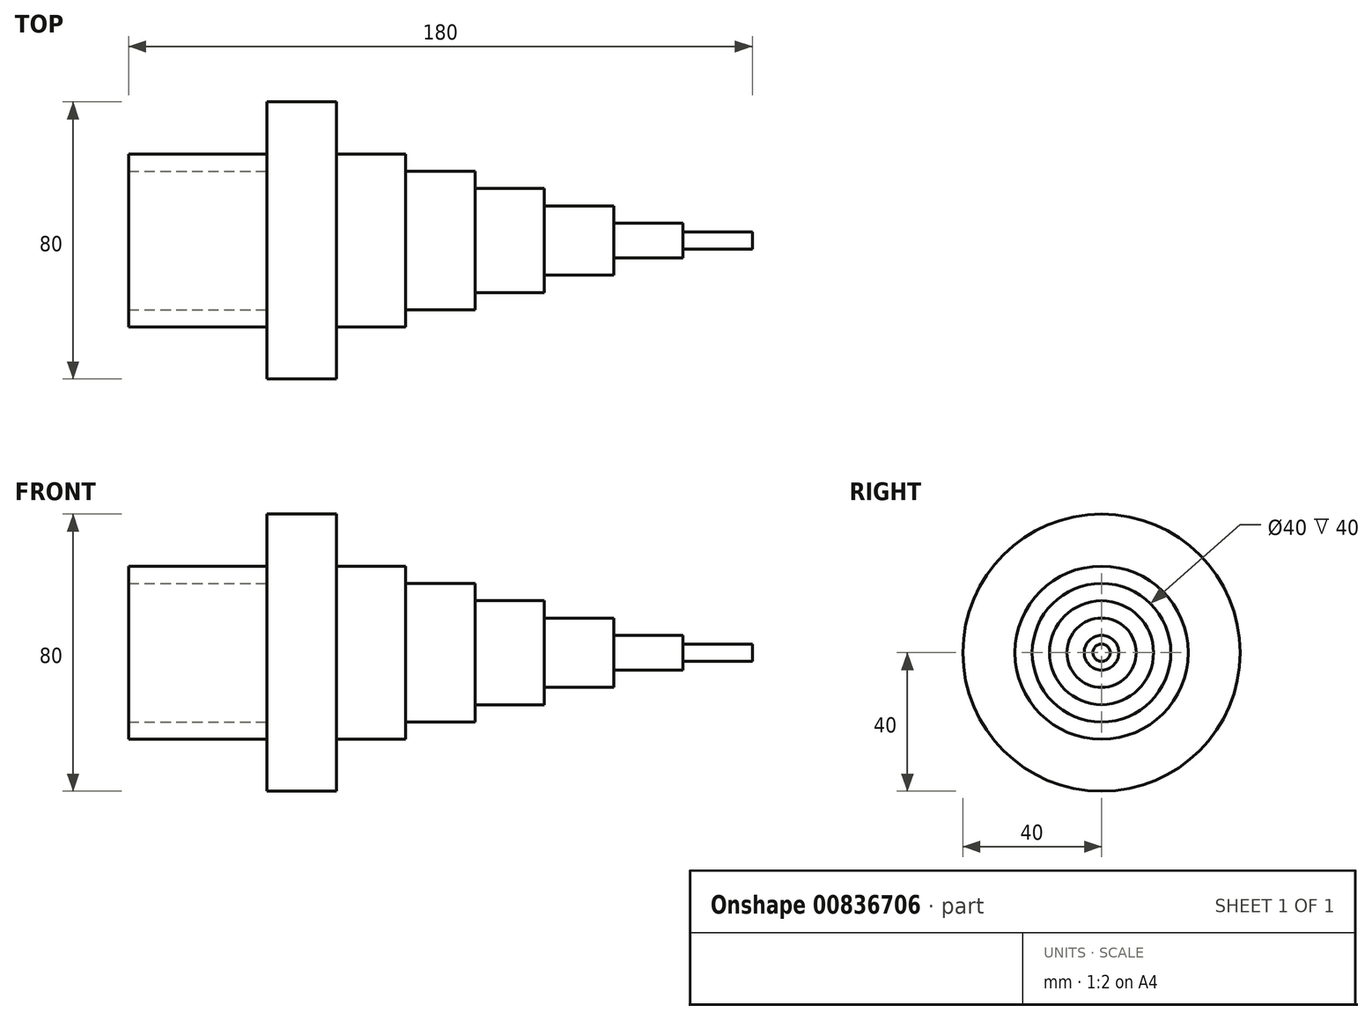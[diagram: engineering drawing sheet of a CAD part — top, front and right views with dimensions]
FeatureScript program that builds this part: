
annotation { "Feature Type Name" : "Feature", "Feature Type Description" : "" }
export const myFeature = defineFeature(function(context is Context, id is Id, definition is map)
    precondition{}
    {
        {
            var Q0;
            Q0=qCreatedBy(makeId("Front.planeOp"),FACE);
            var sketch = newSketch(context, id + "F0", { "sketchPlane" : qUnion([Q0])});
            skLineSegment(sketch, "E0", {"start": v(-45.8, 0) * mm, "end": v(-45.8, 25) * mm});
            skLineSegment(sketch, "E1", {"start": v(-45.8, 25) * mm, "end": v(-5.8, 25) * mm});
            skLineSegment(sketch, "E2", {"start": v(-5.8, 40) * mm, "end": v(-5.8, 25) * mm});
            skLineSegment(sketch, "E3", {"start": v(-5.8, 40) * mm, "end": v(14.2, 40) * mm});
            skLineSegment(sketch, "E4", {"start": v(14.2, 40) * mm, "end": v(14.2, 25) * mm});
            skLineSegment(sketch, "E5", {"start": v(14.2, 25) * mm, "end": v(34.2, 25) * mm});
            skLineSegment(sketch, "E6", {"start": v(34.2, 25) * mm, "end": v(34.2, 20) * mm});
            skLineSegment(sketch, "E7", {"start": v(34.2, 20) * mm, "end": v(54.2, 20) * mm});
            skLineSegment(sketch, "E8", {"start": v(54.2, 20) * mm, "end": v(54.2, 15) * mm});
            skLineSegment(sketch, "E9", {"start": v(54.2, 15) * mm, "end": v(74.2, 15) * mm});
            skLineSegment(sketch, "E10", {"start": v(74.2, 15) * mm, "end": v(74.2, 10) * mm});
            skLineSegment(sketch, "E11", {"start": v(74.2, 10) * mm, "end": v(94.2, 10) * mm});
            skLineSegment(sketch, "E12", {"start": v(94.2, 10) * mm, "end": v(94.2, 5) * mm});
            skLineSegment(sketch, "E13", {"start": v(94.2, 5) * mm, "end": v(114.2, 5) * mm});
            skLineSegment(sketch, "E14", {"start": v(114.2, 5) * mm, "end": v(114.2, 2.5) * mm});
            skLineSegment(sketch, "E15", {"start": v(114.2, 2.5) * mm, "end": v(134.2, 2.5) * mm});
            skLineSegment(sketch, "E16", {"start": v(134.2, 2.5) * mm, "end": v(134.2, 0) * mm});
            skLineSegment(sketch, "E17", {"start": v(134.2, 0) * mm, "end": v(-45.8, 0) * mm});
            skLineSegment(sketch, "E18", {"start": v(-45.8, 0) * mm, "end": v(-45.8, 20) * mm});
            skLineSegment(sketch, "E19", {"start": v(-45.8, 20) * mm, "end": v(-5.8, 20) * mm});
            skLineSegment(sketch, "E20", {"start": v(-5.8, 20) * mm, "end": v(-5.8, 0) * mm});
            skLineSegment(sketch, "E21", {"start": v(-5.8, 0) * mm, "end": v(-45.8, 0) * mm});
            skSolve(sketch);
        }
        {
            var Q0;
            {var subQ0=sQuery(id+"F0.wireOp",EDGE,"E1");Q0=makeQuery(id+"F0.imprint","IMPRINT",FACE,{"disambiguationData":[TD([[makeQuery(id+"F0.imprint","IMPRINT",EDGE,{"derivedFrom":subQ0}),-1.0]])]});}
            var Q1;
            Q1=sQuery(id+"F0.wireOp",EDGE,"E17");
            revolve(context, id + "F1", {"surfaceOperationType" : NewSurfaceOperationType.NEW, "entities" : qUnion([Q0]), "axis" : qUnion([Q1]), "revolveType" : RevolveType.FULL});
        }
        {
            var Q0;
            Q0=sQuery(id+"F0.wireOp",EDGE,"E19");
            var Q1;
            Q1=makeQuery(id+"F1.opRevolve","SWEPT_EDGE",EDGE,{"disambiguationData":[OSD([sQuery(id+"F0.wireOp",EDGE,"E3"),sQuery(id+"F0.wireOp",EDGE,"E4")])]});
            revolve(context, id + "F2", {"bodyType" : ToolBodyType.SURFACE, "surfaceOperationType" : NewSurfaceOperationType.NEW, "surfaceEntities" : qUnion([Q0]), "axis" : qUnion([Q1]), "revolveType" : RevolveType.FULL});
        }
    });
